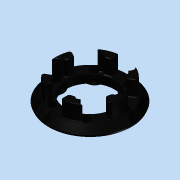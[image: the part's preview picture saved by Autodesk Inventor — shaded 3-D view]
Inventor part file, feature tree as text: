
AUTODESK INVENTOR PART (.ipt)
format: ipt  version: 2015 (Build 190159000, 159)  size: 1,015,808 bytes
history: native  units: in
note: dims shown in document units (in); Inventor stores cm internally (conversion verified against a paired STEP export)
features: chamfer x8, extrude x7, projected_geometry x6, fillet x5, sketch x3, plane x2, split x2, other x1, pattern_circular x1
ambient origin geometry x8: Origin, YZ Plane, XZ Plane, XY Plane, X Axis, Y Axis, Z Axis, Center Point
bodies: Solid1 (feature_tree)
feature tree (35):
  other  "wheelinsertsketch.ipt"
  extrude  "Extrusion1"  Depth=0.3937in TaperAngle=0.0deg
  extrude  "Extrusion2"  Depth=0.25in TaperAngle=0.0deg
  chamfer  "Chamfer1"  Distance=0.25in Angle=45.0deg
  chamfer  "Chamfer6"  Distance=0.1625in Angle=45.0deg
  extrude  "Extrusion6"  Depth=0.0787in
  extrude  "Extrusion9"  Depth=0.0787in
  sketch  "Sketch6"  dims[d3=2.15in d4=0.25in d5=0.0in d6=0.25in d7=0.125in d8=45.0deg d42=0.1625in d43=0.125in d44=45.0deg]
  extrude  "Extrusion7"  Depth=0.0787in
  chamfer  "Chamfer9"  Distance=0.375in
  fillet  "Fillet6"  Radius=0.375in
  fillet  "Fillet7"  Radius=0.375in
  extrude  "Extrusion10"  Depth=0.0787in TaperAngle=0.0deg
  chamfer  "Chamfer10"  Distance=0.01in
  extrude  "Extrusion11"  Depth=0.0787in
  chamfer  "Chamfer11"  Distance=2.3622in Angle=360.0deg
  chamfer  "Chamfer13"  Distance=0.02in
  chamfer  "Chamfer15"  Distance=0.047in Angle=45.0deg
  pattern_circular  "Circular Pattern1"  [2 undecoded]
  chamfer  "Chamfer12"  Distance=0.145in
  fillet  "Fillet8"  Radius=0.05in
  plane  "Work Plane1"
  split  "Split1"
  plane  "Work Plane2"
  split  "Split2"
  fillet  "Fillet10"  Radius=0.05in
  fillet  "Fillet11"  Radius=0.0197in
  sketch  "Sketch5"  dims[d0=0.3937in d1=0.35in d2=0.0in]
  projected_geometry  "Projected Loop3"
  projected_geometry  "Projected Loop4"
  projected_geometry  "Projected Loop5"
  projected_geometry  "Projected Loop12"
  sketch  "Sketch9"  dims[d45=1.0in d46=0.0in d47=0.375in d48=0.375in d49=0.375in d50=0.375in d51=0.375in d52=0.375in d53=0.01in d54=0.0in d67=0.01in d68=0.01in d69=2.3622in d71=360.0deg d73=0.02in d74=0.0in d78=0.047in d79=0.125in d80=45.0deg d81=0.15in d82=0.145in d83=0.05in d84=0.0in d85=0.05in d86=0.125in d87=45.0deg d89=0.0197in d90=0.0in d91=0.0157in d92=0.125in d93=45.0deg d94=0.0098in d95=0.125in d96=45.0deg d97=2.0in d98=2.3622in d99=360.0deg d101=0.0in d106=0.0118in d107=0.125in d108=45.0deg d113=2.3622in d115=360.0deg d118=0.0197in d120=-0.07in d121=0.1in d122=0.0in d123=0.16in d124=0.0787in d125=0.0157in d126=0.125in d127=45.0deg]
  projected_geometry  "Projected Loop13"
  projected_geometry  "Project Cut Edges3"
note: 2 required parameter values undecoded (feature->parameter linkage not recoverable at this tier; creation-order binding heuristic only, values carry confidence <= 0.55)
